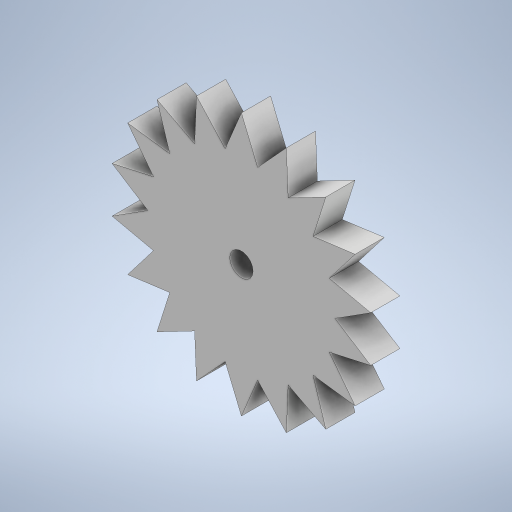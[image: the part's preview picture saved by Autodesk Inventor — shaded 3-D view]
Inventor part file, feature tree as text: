
AUTODESK INVENTOR PART (.ipt)
format: ipt  version: 2023 (Build 270158030, 158C)  size: 285,184 bytes
history: native  units: in
note: dims shown in document units (in); Inventor stores cm internally (conversion verified against a paired STEP export)
features: sketch x3, extrude x2, pattern_circular x1, hole x1
ambient origin geometry x8: Origin, YZ Plane, XZ Plane, XY Plane, X Axis, Y Axis, Z Axis, Center Point
bodies: Solid1 (feature_tree)
feature tree (7):
  extrude  "Extrusion1"  Depth=0.1969in TaperAngle=0.0deg
  extrude  "Extrusion2"  Depth=0.3937in
  pattern_circular  "Circular Pattern1"  Count=18 Angle=360.0deg
  hole  "Hole1"  [1 undecoded]
  sketch  "Sketch2"  dims[d0=0.9843in d1=0.1969in d2=0.0in]
  sketch  "Sketch3"  dims[d3=45.0deg d4=0.3937in]
  sketch  "Sketch4"  dims[d5=0.0in d6=0.0in d7=7.0866in d8=360.0deg d10=0.1575in d11=0.6299in d12=0.1575in d13=0.0787in d14=90.0deg d15=1.0748in d16=0.8108in]
note: 1 required parameter value undecoded (feature->parameter linkage not recoverable at this tier; creation-order binding heuristic only, values carry confidence <= 0.55)
